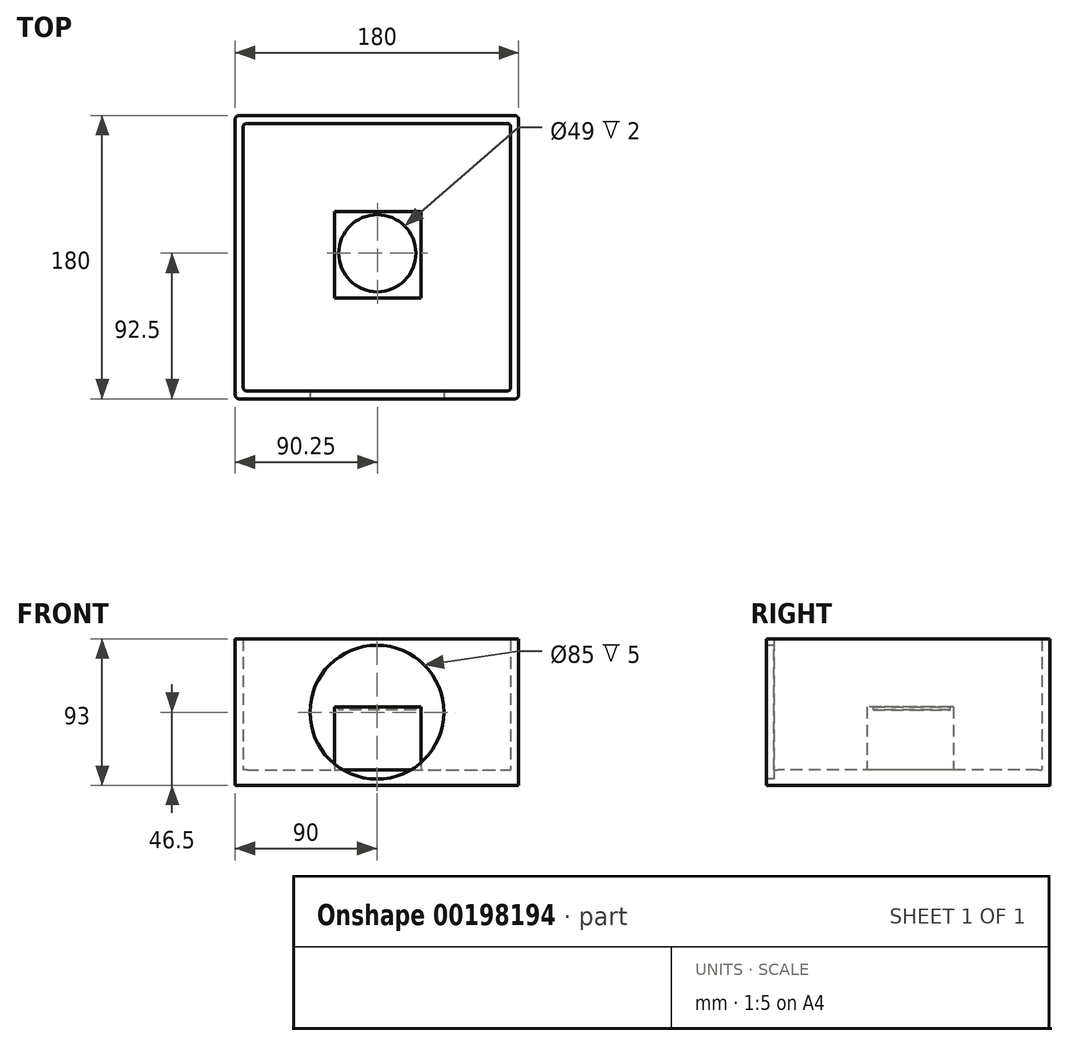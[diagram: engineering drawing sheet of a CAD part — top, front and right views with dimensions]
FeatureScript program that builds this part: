
annotation { "Feature Type Name" : "Feature", "Feature Type Description" : "" }
export const myFeature = defineFeature(function(context is Context, id is Id, definition is map)
    precondition{}
    {
        {
            var Q0;
            Q0=qCreatedBy(makeId("Top.planeOp"),FACE);
            var sketch = newSketch(context, id + "F0", { "sketchPlane" : qUnion([Q0])});
            skLineSegment(sketch, "E0.bottom", {"start": v(-90, 90) * mm, "end": v(90, 90) * mm});
            skLineSegment(sketch, "E0.top", {"start": v(-90, -90) * mm, "end": v(90, -90) * mm});
            skLineSegment(sketch, "E0.left", {"start": v(-90, 90) * mm, "end": v(-90, -90) * mm});
            skLineSegment(sketch, "E0.right", {"start": v(90, 90) * mm, "end": v(90, -90) * mm});
            skPoint(sketch, "E0.middle", {"position": v(0, 0) * mm});
            skSolve(sketch);
        }
        {
            var Q0;
            Q0 = qSketchRegion(id + "F0", true);
            extrude(context, id + "F1", {"entities" : qUnion([Q0]), "depth" : 10 * mm});
        }
        {
            var Q0;
            Q0=makeQuery(id+"F1.opExtrude","CAP_FACE",FACE,{"disambiguationData":[OSD([sQuery(id+"F0.wireOp",EDGE,"E0.bottom"),sQuery(id+"F0.wireOp",EDGE,"E0.top"),sQuery(id+"F0.wireOp",EDGE,"E0.left"),sQuery(id+"F0.wireOp",EDGE,"E0.right")])],"isStart":false});
            var sketch = newSketch(context, id + "F2", { "sketchPlane" : qUnion([Q0])});
            skLineSegment(sketch, "E1.bottom", {"start": v(-27, 29) * mm, "end": v(28, 29) * mm});
            skLineSegment(sketch, "E1.top", {"start": v(-27, -26) * mm, "end": v(28, -26) * mm});
            skLineSegment(sketch, "E1.left", {"start": v(-27, 29) * mm, "end": v(-27, -26) * mm});
            skLineSegment(sketch, "E1.right", {"start": v(28, 29) * mm, "end": v(28, -26) * mm});
            skPoint(sketch, "E1.middle", {"position": v(0.5, 1.5) * mm});
            skSolve(sketch);
        }
        {
            var Q0;
            Q0 = qSketchRegion(id + "F2", true);
            extrude(context, id + "F3", {"entities" : qUnion([Q0]), "operationType" : NewBodyOperationType.ADD, "depth" : 40 * mm});
        }
        {
            var Q0;
            Q0=makeQuery(id+"F1.opExtrude","CAP_FACE",FACE,{"disambiguationData":[OSD([sQuery(id+"F0.wireOp",EDGE,"E0.bottom"),sQuery(id+"F0.wireOp",EDGE,"E0.top"),sQuery(id+"F0.wireOp",EDGE,"E0.left"),sQuery(id+"F0.wireOp",EDGE,"E0.right")])],"isStart":false});
            var sketch = newSketch(context, id + "F4", { "sketchPlane" : qUnion([Q0])});
            skLineSegment(sketch, "E2.bottom", {"start": v(-90, 90) * mm, "end": v(90, 90) * mm});
            skLineSegment(sketch, "E2.top", {"start": v(-90, -90) * mm, "end": v(90, -90) * mm});
            skLineSegment(sketch, "E2.left", {"start": v(-90, 90) * mm, "end": v(-90, -90) * mm});
            skLineSegment(sketch, "E2.right", {"start": v(90, 90) * mm, "end": v(90, -90) * mm});
            skPoint(sketch, "E2.middle", {"position": v(0, 0) * mm});
            skLineSegment(sketch, "E3.bottom", {"start": v(-85, 85) * mm, "end": v(85, 85) * mm});
            skLineSegment(sketch, "E3.top", {"start": v(-85, -85) * mm, "end": v(85, -85) * mm});
            skLineSegment(sketch, "E3.left", {"start": v(-85, 85) * mm, "end": v(-85, -85) * mm});
            skLineSegment(sketch, "E3.right", {"start": v(85, 85) * mm, "end": v(85, -85) * mm});
            skSolve(sketch);
        }
        {
            var Q0;
            Q0 = qSketchRegion(id + "F4", true);
            extrude(context, id + "F5", {"entities" : qUnion([Q0]), "operationType" : NewBodyOperationType.ADD, "depth" : 83 * mm});
        }
        {
            var Q0;
            Q0=makeQuery(id+"F3.opExtrude","CAP_FACE",FACE,{"disambiguationData":[OSD([sQuery(id+"F2.wireOp",EDGE,"E1.bottom"),sQuery(id+"F2.wireOp",EDGE,"E1.top"),sQuery(id+"F2.wireOp",EDGE,"E1.left"),sQuery(id+"F2.wireOp",EDGE,"E1.right")])],"isStart":false});
            var sketch = newSketch(context, id + "F6", { "sketchPlane" : qUnion([Q0])});
            skLineSegment(sketch, "E4", {"start": v(0.5, 17) * mm, "end": v(0, -12) * mm, "construction": true});
            skCircle(sketch, "E5", {"center": v(0.25, 2.5) * mm, "radius": 24.5 * mm});
            skSolve(sketch);
        }
        {
            var Q0;
            Q0=makeQuery(id+"F6.imprint","IMPRINT",FACE,{"disambiguationData":[TD([[makeQuery(id+"F6.imprint","IMPRINT",EDGE,{"derivedFrom":sQuery(id+"F6.wireOp",EDGE,"E5")}),1.0]])]});
            var Q1;
            Q1=sQuery(id+"F6.wireOp",EDGE,"E5");
            extrude(context, id + "F7", {"entities" : qUnion([Q0]), "operationType" : NewBodyOperationType.REMOVE, "surfaceEntities" : qUnion([Q1]), "oppositeDirection" : true, "depth" : 2 * mm});
        }
        {
            var Q0;
            Q0=makeQuery(id+"F5.boolean.opBoolean","MERGE",FACE,{"derivedFrom":[makeQuery(id+"F1.opExtrude","SWEPT_FACE",FACE,{"disambiguationData":[OSD([sQuery(id+"F0.wireOp",EDGE,"E0.top")])]}),makeQuery(id+"F5.opExtrude","SWEPT_FACE",FACE,{"disambiguationData":[OSD([sQuery(id+"F4.wireOp",EDGE,"E2.top")])]})]});
            var sketch = newSketch(context, id + "F8", { "sketchPlane" : qUnion([Q0])});
            skLineSegment(sketch, "E6", {"start": v(0, 93) * mm, "end": v(0, 0) * mm, "construction": true});
            skCircle(sketch, "E7", {"center": v(0, 46.5) * mm, "radius": 42.5 * mm});
            skSolve(sketch);
        }
        {
            var Q0;
            Q0 = qSketchRegion(id + "F8", true);
            extrude(context, id + "F9", {"entities" : qUnion([Q0]), "operationType" : NewBodyOperationType.REMOVE, "oppositeDirection" : true, "depth" : 5 * mm});
        }
        {
            var Q0;
            Q0=makeQuery(id+"F5.boolean.opBoolean","MERGE",EDGE,{"derivedFrom":[makeQuery(id+"F1.opExtrude","SWEPT_EDGE",EDGE,{"disambiguationData":[OSD([sQuery(id+"F0.wireOp",EDGE,"E0.bottom"),sQuery(id+"F0.wireOp",EDGE,"E0.right")])]}),makeQuery(id+"F5.opExtrude","SWEPT_EDGE",EDGE,{"disambiguationData":[OSD([sQuery(id+"F4.wireOp",EDGE,"E2.bottom"),sQuery(id+"F4.wireOp",EDGE,"E2.right")])]})]});
            var Q1;
            Q1=makeQuery(id+"F5.boolean.opBoolean","MERGE",EDGE,{"derivedFrom":[makeQuery(id+"F1.opExtrude","SWEPT_EDGE",EDGE,{"disambiguationData":[OSD([sQuery(id+"F0.wireOp",EDGE,"E0.bottom"),sQuery(id+"F0.wireOp",EDGE,"E0.left")])]}),makeQuery(id+"F5.opExtrude","SWEPT_EDGE",EDGE,{"disambiguationData":[OSD([sQuery(id+"F4.wireOp",EDGE,"E2.bottom"),sQuery(id+"F4.wireOp",EDGE,"E2.left")])]})]});
            var Q2;
            Q2=makeQuery(id+"F5.boolean.opBoolean","MERGE",EDGE,{"derivedFrom":[makeQuery(id+"F1.opExtrude","SWEPT_EDGE",EDGE,{"disambiguationData":[OSD([sQuery(id+"F0.wireOp",EDGE,"E0.top"),sQuery(id+"F0.wireOp",EDGE,"E0.right")])]}),makeQuery(id+"F5.opExtrude","SWEPT_EDGE",EDGE,{"disambiguationData":[OSD([sQuery(id+"F4.wireOp",EDGE,"E2.top"),sQuery(id+"F4.wireOp",EDGE,"E2.right")])]})]});
            var Q3;
            Q3=makeQuery(id+"F5.boolean.opBoolean","MERGE",EDGE,{"derivedFrom":[makeQuery(id+"F1.opExtrude","SWEPT_EDGE",EDGE,{"disambiguationData":[OSD([sQuery(id+"F0.wireOp",EDGE,"E0.top"),sQuery(id+"F0.wireOp",EDGE,"E0.left")])]}),makeQuery(id+"F5.opExtrude","SWEPT_EDGE",EDGE,{"disambiguationData":[OSD([sQuery(id+"F4.wireOp",EDGE,"E2.top"),sQuery(id+"F4.wireOp",EDGE,"E2.left")])]})]});
            fillet(context, id + "F10", {"entities" : qUnion([Q0, Q1, Q2, Q3]), "radius" : 2.5 * mm, "tangentPropagation" : true, "allowEdgeOverflow" : false});
        }
        {
            var Q0;
            Q0=makeQuery(id+"F5.opExtrude","SWEPT_EDGE",EDGE,{"disambiguationData":[OSD([sQuery(id+"F4.wireOp",EDGE,"E3.bottom"),sQuery(id+"F4.wireOp",EDGE,"E3.left")])]});
            var Q1;
            Q1=makeQuery(id+"F5.opExtrude","SWEPT_EDGE",EDGE,{"disambiguationData":[OSD([sQuery(id+"F4.wireOp",EDGE,"E3.bottom"),sQuery(id+"F4.wireOp",EDGE,"E3.right")])]});
            var Q2;
            Q2=makeQuery(id+"F5.opExtrude","SWEPT_EDGE",EDGE,{"disambiguationData":[OSD([sQuery(id+"F4.wireOp",EDGE,"E3.top"),sQuery(id+"F4.wireOp",EDGE,"E3.left")])]});
            var Q3;
            Q3=makeQuery(id+"F5.opExtrude","SWEPT_EDGE",EDGE,{"disambiguationData":[OSD([sQuery(id+"F4.wireOp",EDGE,"E3.top"),sQuery(id+"F4.wireOp",EDGE,"E3.right")])]});
            fillet(context, id + "F11", {"entities" : qUnion([Q0, Q1, Q2, Q3]), "radius" : 2.5 * mm, "tangentPropagation" : true, "allowEdgeOverflow" : false});
        }
    });
